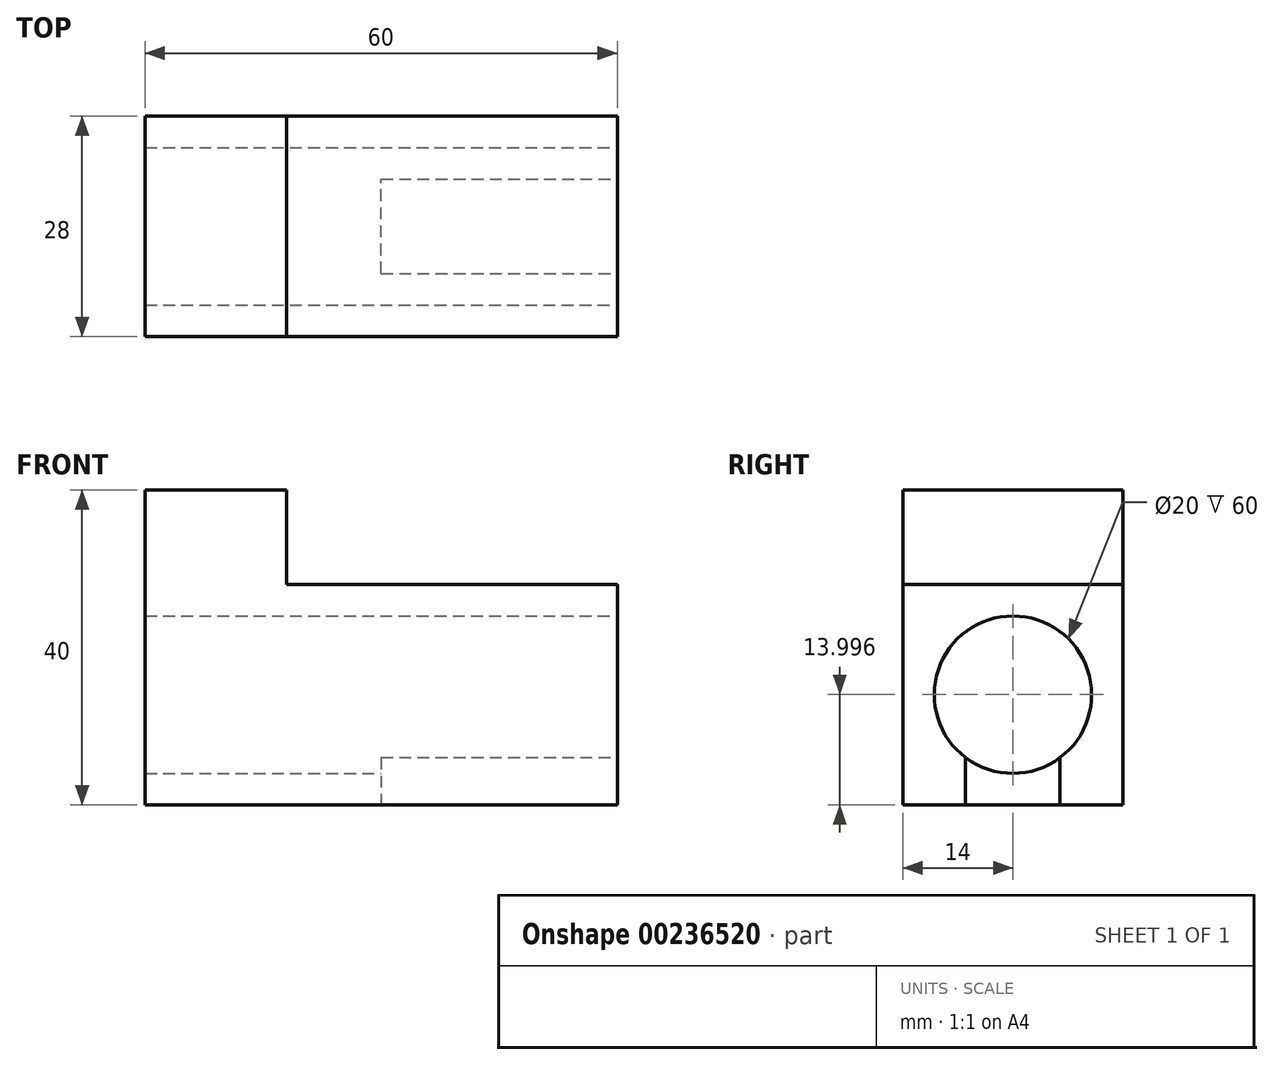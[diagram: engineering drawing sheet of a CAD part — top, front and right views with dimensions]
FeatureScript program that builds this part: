
annotation { "Feature Type Name" : "Feature", "Feature Type Description" : "" }
export const myFeature = defineFeature(function(context is Context, id is Id, definition is map)
    precondition{}
    {
        {
            var Q0;
            Q0=qCreatedBy(makeId("Front.planeOp"),FACE);
            var sketch = newSketch(context, id + "F0", { "sketchPlane" : qUnion([Q0])});
            skLineSegment(sketch, "E0", {"start": v(4.86, -47.07) * mm, "end": v(-55.14, -47.07) * mm});
            skLineSegment(sketch, "E1", {"start": v(-37.14, -19.07) * mm, "end": v(4.86, -19.07) * mm});
            skLineSegment(sketch, "E2", {"start": v(4.86, -19.07) * mm, "end": v(4.86, -47.07) * mm});
            skLineSegment(sketch, "E3", {"start": v(-55.14, -7.07) * mm, "end": v(-37.14, -7.07) * mm});
            skLineSegment(sketch, "E4", {"start": v(-37.14, -7.07) * mm, "end": v(-37.14, -19.07) * mm});
            skPoint(sketch, "E5.end.orphan", {"position": v(-55.14, -19.07) * mm});
            skLineSegment(sketch, "E6", {"start": v(-55.14, -47.07) * mm, "end": v(-55.14, -7.07) * mm});
            skSolve(sketch);
        }
        {
            var Q0;
            Q0=makeQuery(id+"F0.imprint","IMPRINT",FACE,{"disambiguationData":[TD([[makeQuery(id+"F0.imprint","IMPRINT",EDGE,{"derivedFrom":sQuery(id+"F0.wireOp",EDGE,"E0")}),-1.0]])]});
            extrude(context, id + "F1", {"entities" : qUnion([Q0]), "endBound" : BoundingType.SYMMETRIC, "depth" : 28 * mm});
        }
        {
            var Q0;
            Q0=makeQuery(id+"F1.opExtrude","SWEPT_FACE",FACE,{"disambiguationData":[OSD([sQuery(id+"F0.wireOp",EDGE,"E2")])]});
            var sketch = newSketch(context, id + "F2", { "sketchPlane" : qUnion([Q0])});
            skLineSegment(sketch, "E7", {"start": v(-14, -33.07) * mm, "end": v(14, -33.07) * mm, "construction": true});
            skCircle(sketch, "E8", {"center": v(0, -33.07) * mm, "radius": 10 * mm});
            skLineSegment(sketch, "E9", {"start": v(0, -19.07) * mm, "end": v(0, -47.07) * mm, "construction": true});
            skSolve(sketch);
        }
        {
            var Q0;
            Q0 = qSketchRegion(id + "F2", true);
            extrude(context, id + "F3", {"entities" : qUnion([Q0]), "operationType" : NewBodyOperationType.REMOVE, "endBound" : BoundingType.THROUGH_ALL, "oppositeDirection" : true, "depth" : 85 * mm});
        }
        {
            var Q0;
            Q0=makeQuery(id+"F1.opExtrude","SWEPT_FACE",FACE,{"disambiguationData":[OSD([sQuery(id+"F0.wireOp",EDGE,"E2")])]});
            var sketch = newSketch(context, id + "F4", { "sketchPlane" : qUnion([Q0])});
            skLineSegment(sketch, "E10", {"start": v(0, -19.07) * mm, "end": v(0, -47.07) * mm, "construction": true});
            skLineSegment(sketch, "E11.0", {"start": v(6, -19.07) * mm, "end": v(6, -47.07) * mm});
            skLineSegment(sketch, "E12.MirrorCS", {"start": v(-6, -19.07) * mm, "end": v(-6, -47.07) * mm});
            skLineSegment(sketch, "E13", {"start": v(-6, -19.07) * mm, "end": v(6, -19.07) * mm, "construction": true});
            skLineSegment(sketch, "E14", {"start": v(-6, -47.07) * mm, "end": v(6, -47.07) * mm});
            skSolve(sketch);
        }
        {
            var Q0;
            {var subQ0=sQuery(id+"F4.wireOp",EDGE,"E11.0");var subQ3=makeQuery(id+"F3.boolean.opBoolean","COPY",EDGE,{"derivedFrom":makeQuery(id+"F3.opExtrude","CAP_EDGE",EDGE,{"disambiguationData":[OSD([sQuery(id+"F2.wireOp",EDGE,"E8")])],"isStart":true})});var subQ4=makeQuery(id+"F4.imprint","INTERSECT",VERTEX,{"disambiguationData":[OD(0.0)],"derivedFrom":[subQ3,subQ0]});Q0=makeQuery(id+"F4.imprint","IMPRINT",FACE,{"disambiguationData":[TD([[makeQuery(id+"F4.imprint","IMPRINT",EDGE,{"disambiguationData":[TD([[subQ4,-1.0]])],"derivedFrom":subQ3}),-1.0]])]});}
            var Q1;
            {var subQ0=sQuery(id+"F4.wireOp",EDGE,"E14");Q1=makeQuery(id+"F4.imprint","IMPRINT",FACE,{"disambiguationData":[TD([[makeQuery(id+"F4.imprint","IMPRINT",EDGE,{"derivedFrom":subQ0}),1.0]])]});}
            extrude(context, id + "F5", {"entities" : qUnion([Q0, Q1]), "operationType" : NewBodyOperationType.REMOVE, "oppositeDirection" : true, "depth" : 30 * mm});
        }
    });
